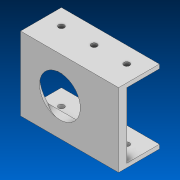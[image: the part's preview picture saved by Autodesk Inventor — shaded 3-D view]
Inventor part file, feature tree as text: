
AUTODESK INVENTOR PART (.ipt)
format: ipt  version: 2022.2 (Build 262287000, 287)  size: 145,920 bytes
history: native  units: in
note: dims shown in document units (in); Inventor stores cm internally (conversion verified against a paired STEP export)
features: sketch x4, extrude x3, chamfer x1, hole x1
ambient origin geometry x8: Origin, YZ Plane, XZ Plane, XY Plane, X Axis, Y Axis, Z Axis, Center Point
bodies: Solid1 (feature_tree)
feature tree (9):
  extrude  "Extrusion1"  Depth=1.25in
  chamfer  "Chamfer1"  Distance=1.0in
  extrude  "Extrusion2"  Depth=0.75in
  hole  "Hole1"  [1 undecoded]
  extrude  "Extrusion3"  Depth=0.75in TaperAngle=45.0deg
  sketch  "Sketch1"  dims[d0=1.25in d1=2.0in]
  sketch  "Sketch2"  dims[d3=0.2965in]
  sketch  "Sketch3"  dims[d6=1.5in]
  sketch  "Sketch4"  dims[d7=1.5in d8=1.0in d9=1.0in d10=0.25in d11=0.0in d12=0.25in d13=0.25in d14=45.0deg d15=0.125in d16=1.0in d17=0.25in d18=0.0in d19=0.5in d20=1.0in d21=1.0in d22=0.5in d23=0.175in d24=0.75in d25=0.375in d26=0.25in d27=0.5635in d28=1.0in d29=0.8108in d30=1.0in d31=0.0in]
note: 1 required parameter value undecoded (feature->parameter linkage not recoverable at this tier; creation-order binding heuristic only, values carry confidence <= 0.55)
